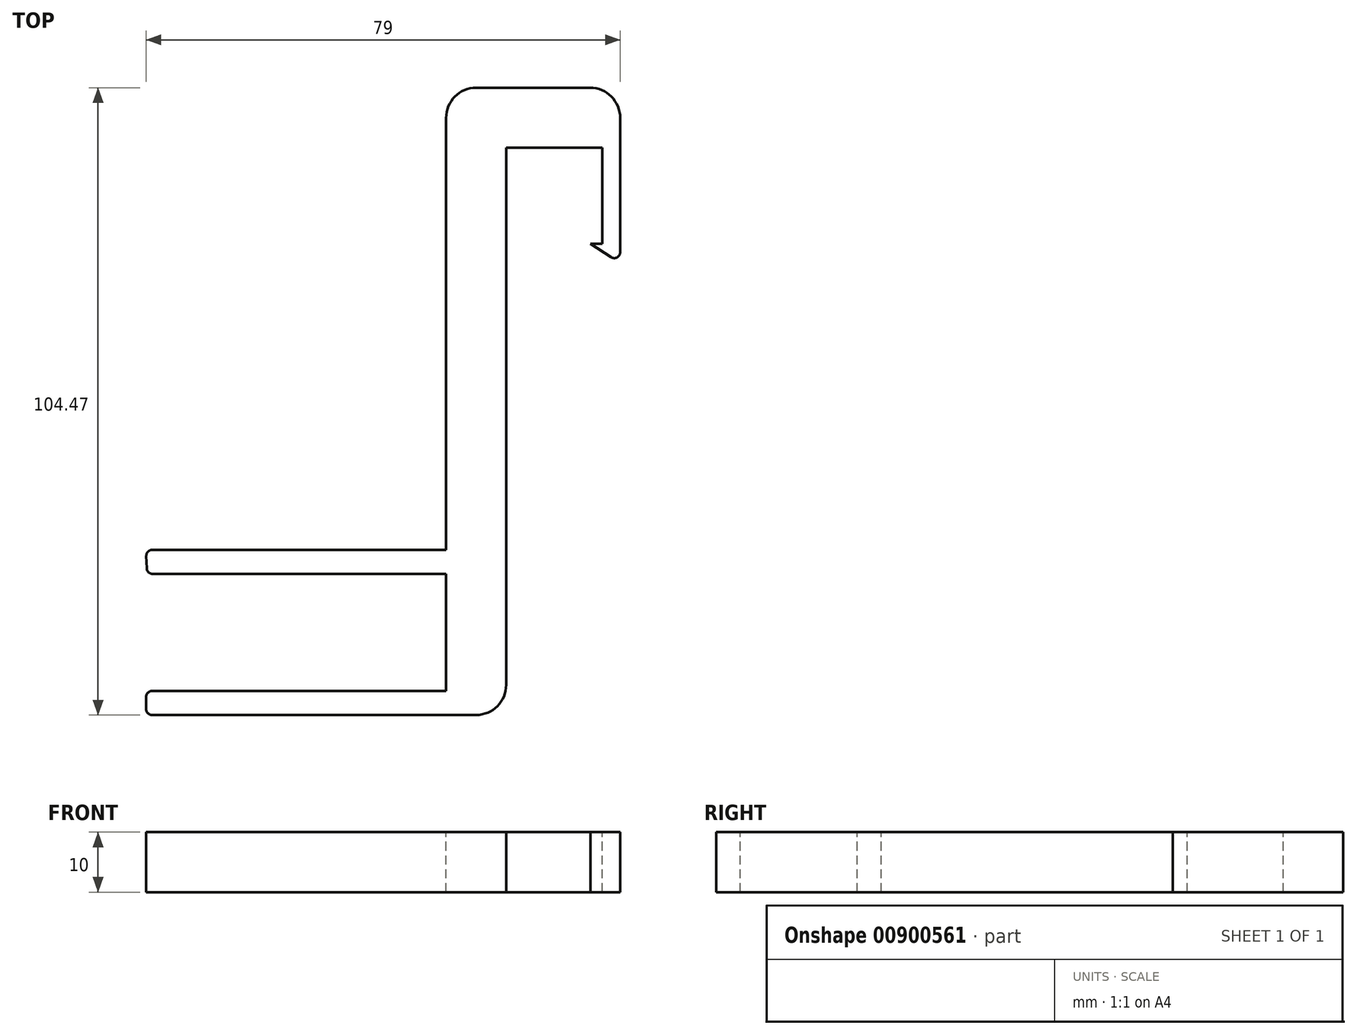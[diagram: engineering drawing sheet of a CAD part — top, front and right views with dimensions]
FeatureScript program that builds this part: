
annotation { "Feature Type Name" : "Feature", "Feature Type Description" : "" }
export const myFeature = defineFeature(function(context is Context, id is Id, definition is map)
    precondition{}
    {
        {
            var Q0;
            Q0=qCreatedBy(makeId("Top.planeOp"),FACE);
            var sketch = newSketch(context, id + "F0", { "sketchPlane" : qUnion([Q0])});
            skLineSegment(sketch, "E0.left", {"start": v(0, 0) * mm, "end": v(0, 75.97) * mm});
            skLineSegment(sketch, "E0.right", {"start": v(10, -18.5) * mm, "end": v(10, 71) * mm});
            skLineSegment(sketch, "E1.bottom", {"start": v(10, 71) * mm, "end": v(26, 71) * mm});
            skLineSegment(sketch, "E1.top", {"start": v(5, 80.97) * mm, "end": v(24, 80.97) * mm});
            skLineSegment(sketch, "E2.bottom", {"start": v(26, 71) * mm, "end": v(29, 71) * mm});
            skLineSegment(sketch, "E2.top", {"start": v(26, 55) * mm, "end": v(29, 55) * mm});
            skLineSegment(sketch, "E2.left", {"start": v(26, 71) * mm, "end": v(26, 55) * mm});
            skLineSegment(sketch, "E2.right", {"start": v(29, 71) * mm, "end": v(29, 55) * mm});
            skLineSegment(sketch, "E3", {"start": v(26, 55) * mm, "end": v(24.07, 55) * mm});
            skLineSegment(sketch, "E4", {"start": v(24.07, 55) * mm, "end": v(27.45, 52.77) * mm});
            skLineSegment(sketch, "E5", {"start": v(29, 53.6) * mm, "end": v(29, 55) * mm});
            skLineSegment(sketch, "E6", {"start": v(29, 75.97) * mm, "end": v(29, 71) * mm});
            skPoint(sketch, "E7.visualSharp", {"position": v(0, 80.97) * mm});
            skArc(sketch, "E7.filletArc", {"start": v(5, 80.97) * mm, "mid": v(1.46, 79.5) * mm, "end": v(0, 75.97) * mm});
            skPoint(sketch, "E8.visualSharp", {"position": v(29, 80.97) * mm});
            skArc(sketch, "E8.filletArc", {"start": v(29, 75.97) * mm, "mid": v(27.54, 79.5) * mm, "end": v(24, 80.97) * mm});
            skLineSegment(sketch, "E9.bottom", {"start": v(0, 0) * mm, "end": v(-48.89, 0) * mm});
            skLineSegment(sketch, "E9.top", {"start": v(0, 4) * mm, "end": v(-48.96, 4) * mm});
            skLineSegment(sketch, "E9.left", {"start": v(0, 0) * mm, "end": v(0, 4) * mm});
            skLineSegment(sketch, "E10.right", {"start": v(0, 0) * mm, "end": v(0, -19.5) * mm});
            skLineSegment(sketch, "E11.bottom", {"start": v(-49, -19.5) * mm, "end": v(0, -19.5) * mm});
            skLineSegment(sketch, "E11.top", {"start": v(-49, -23.5) * mm, "end": v(0, -23.5) * mm});
            skLineSegment(sketch, "E11.left", {"start": v(-50, -20.5) * mm, "end": v(-50, -22.5) * mm});
            skLineSegment(sketch, "E11.right", {"start": v(0, -19.5) * mm, "end": v(0, -23.5) * mm});
            skLineSegment(sketch, "E12", {"start": v(0, -23.5) * mm, "end": v(5, -23.5) * mm});
            skPoint(sketch, "E13.visualSharp", {"position": v(10, -23.5) * mm});
            skArc(sketch, "E13.filletArc", {"start": v(5, -23.5) * mm, "mid": v(8.54, -22.04) * mm, "end": v(10, -18.5) * mm});
            skPoint(sketch, "E14.visualSharp", {"position": v(-50, -23.5) * mm});
            skPoint(sketch, "E15.visualSharp", {"position": v(-50, -19.5) * mm});
            skArc(sketch, "E15.filletArc", {"start": v(-49, -19.5) * mm, "mid": v(-49.7, -19.8) * mm, "end": v(-50, -20.5) * mm});
            skArc(sketch, "E16.filletArc", {"start": v(-50, -22.5) * mm, "mid": v(-49.7, -23.2) * mm, "end": v(-49, -23.5) * mm});
            skPoint(sketch, "E17.visualSharp", {"position": v(29, 51.74) * mm});
            skArc(sketch, "E17.filletArc", {"start": v(27.45, 52.77) * mm, "mid": v(28.47, 52.72) * mm, "end": v(29, 53.6) * mm});
            skLineSegment(sketch, "E18", {"start": v(-49.96, 2.96) * mm, "end": v(-49.89, 0.96) * mm});
            skPoint(sketch, "E19.visualSharp", {"position": v(-50, 4) * mm});
            skArc(sketch, "E19.filletArc", {"start": v(-48.96, 4) * mm, "mid": v(-49.68, 3.7) * mm, "end": v(-49.96, 2.96) * mm});
            skPoint(sketch, "E20.visualSharp", {"position": v(-49.85, 0) * mm});
            skArc(sketch, "E20.filletArc", {"start": v(-49.89, 0.96) * mm, "mid": v(-49.58, 0.28) * mm, "end": v(-48.89, 0) * mm});
            skSolve(sketch);
        }
        {
            var Q0;
            Q0=makeQuery(id+"F0.imprint","IMPRINT",FACE,{"disambiguationData":[TD([[makeQuery(id+"F0.imprint","IMPRINT",EDGE,{"derivedFrom":sQuery(id+"F0.wireOp",EDGE,"E11.bottom")}),-1.0]])]});
            var Q1;
            Q1=makeQuery(id+"F0.imprint","IMPRINT",FACE,{"disambiguationData":[TD([[makeQuery(id+"F0.imprint","IMPRINT",EDGE,{"derivedFrom":sQuery(id+"F0.wireOp",EDGE,"E0.left")}),-1.0]])]});
            var Q2;
            Q2=makeQuery(id+"F0.imprint","IMPRINT",FACE,{"disambiguationData":[TD([[makeQuery(id+"F0.imprint","IMPRINT",EDGE,{"derivedFrom":sQuery(id+"F0.wireOp",EDGE,"E2.bottom")}),-1.0]])]});
            var Q3;
            Q3=makeQuery(id+"F0.imprint","IMPRINT",FACE,{"disambiguationData":[TD([[makeQuery(id+"F0.imprint","IMPRINT",EDGE,{"derivedFrom":sQuery(id+"F0.wireOp",EDGE,"E9.bottom")}),-1.0]])]});
            var Q4;
            Q4=makeQuery(id+"F0.imprint","IMPRINT",FACE,{"disambiguationData":[TD([[makeQuery(id+"F0.imprint","IMPRINT",EDGE,{"derivedFrom":sQuery(id+"F0.wireOp",EDGE,"E2.top")}),-1.0]])]});
            extrude(context, id + "F1", {"entities" : qUnion([Q0, Q1, Q2, Q3, Q4]), "oppositeDirection" : true, "depth" : 10 * mm, "offsetDistance" : 25 * mm});
        }
    });
